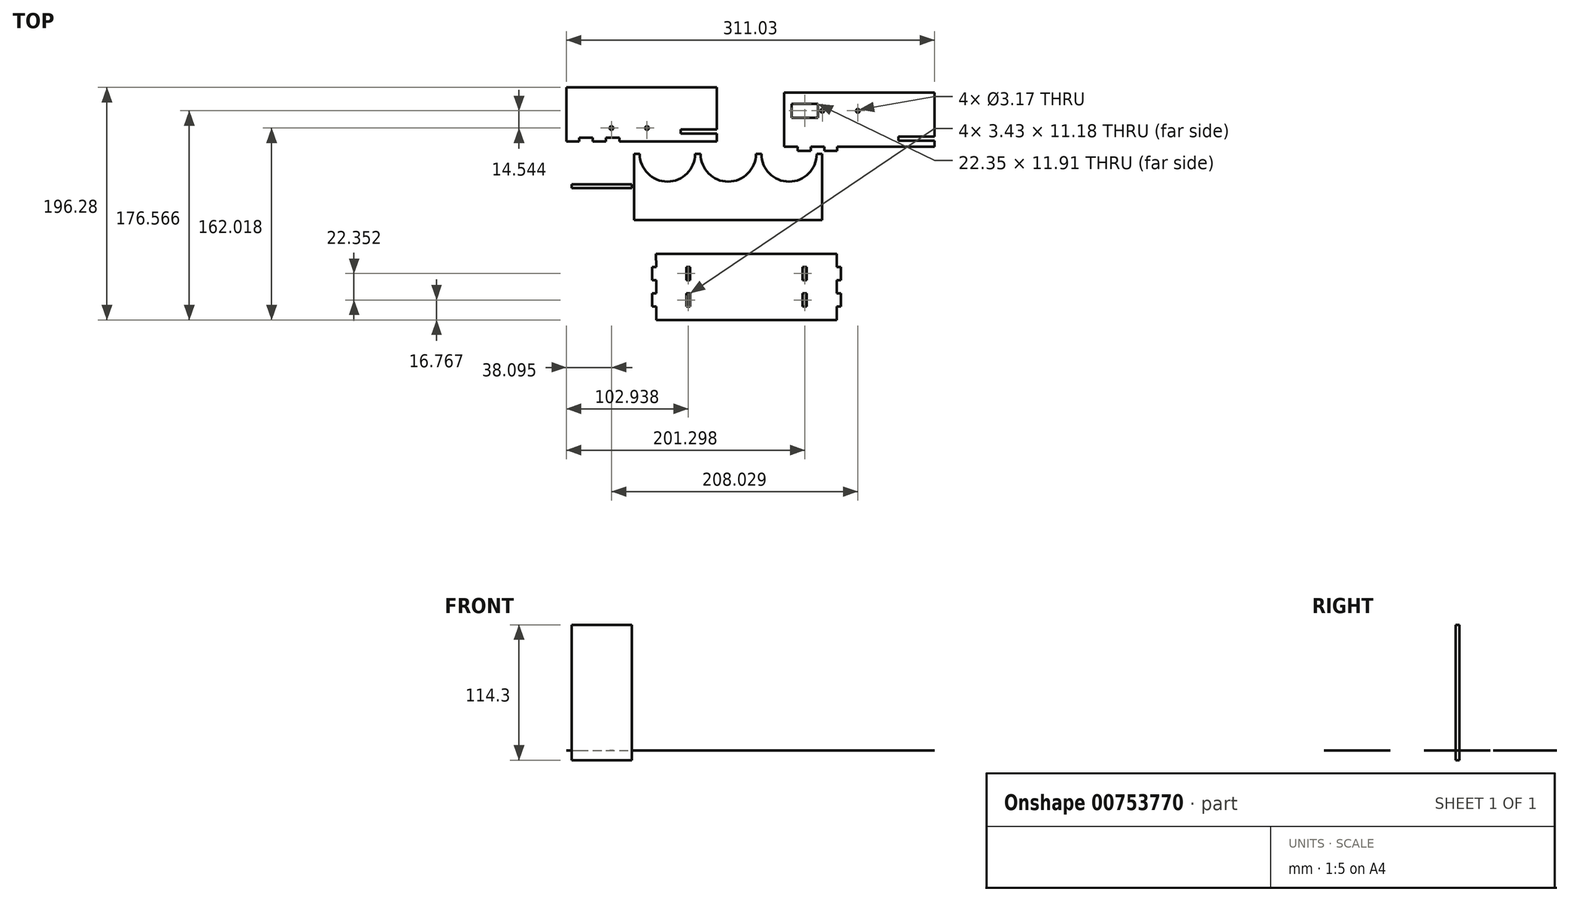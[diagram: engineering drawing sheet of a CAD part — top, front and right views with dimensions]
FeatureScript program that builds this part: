
annotation { "Feature Type Name" : "Feature", "Feature Type Description" : "" }
export const myFeature = defineFeature(function(context is Context, id is Id, definition is map)
    precondition{}
    {
        {
            var Q0;
            Q0=qCreatedBy(makeId("Top.planeOp"),FACE);
            var sketch = newSketch(context, id + "F0", { "sketchPlane" : qUnion([Q0])});
            skLineSegment(sketch, "E0.bottom", {"start": v(-76.72, 25.8) * mm, "end": v(-72.09, 25.8) * mm});
            skLineSegment(sketch, "E0.top", {"start": v(-76.72, -30.08) * mm, "end": v(82.03, -30.08) * mm});
            skLineSegment(sketch, "E0.left", {"start": v(-76.72, 25.8) * mm, "end": v(-76.72, -30.08) * mm});
            skLineSegment(sketch, "E0.right", {"start": v(82.03, 25.8) * mm, "end": v(82.03, -30.08) * mm});
            skArc(sketch, "E1", {"start": v(-20.72, 25.8) * mm, "mid": v(2.65, 2.43) * mm, "end": v(26.02, 25.8) * mm});
            skLineSegment(sketch, "E2.trimOffspring", {"start": v(26.02, 25.8) * mm, "end": v(30.66, 25.8) * mm});
            skArc(sketch, "E3", {"start": v(-72.09, 25.8) * mm, "mid": v(-48.72, 2.43) * mm, "end": v(-25.35, 25.8) * mm});
            skArc(sketch, "E4", {"start": v(30.66, 25.8) * mm, "mid": v(54.02, 2.43) * mm, "end": v(77.4, 25.8) * mm});
            skLineSegment(sketch, "E5.trimOffspring", {"start": v(-25.35, 25.8) * mm, "end": v(-20.72, 25.8) * mm});
            skLineSegment(sketch, "E6.trimOffspring", {"start": v(77.4, 25.8) * mm, "end": v(82.03, 25.8) * mm});
            skSolve(sketch);
        }
        {
            var Q0;
            Q0 = qSketchRegion(id + "F0", true);
            extrude(context, id + "F1", {"entities" : qUnion([Q0]), "depth" : 1 / 203.2 * mm, "offsetDistance" : 25.4 * mm});
        }
        {
            var Q0;
            Q0=qCreatedBy(makeId("Top.planeOp"),FACE);
            var sketch = newSketch(context, id + "F2", { "sketchPlane" : qUnion([Q0])});
            skLineSegment(sketch, "E7.bottom", {"start": v(-134.04, 81.95) * mm, "end": v(-7.04, 81.95) * mm});
            skLineSegment(sketch, "E7.top", {"start": v(-134.04, 36.23) * mm, "end": v(-123.12, 36.23) * mm});
            skLineSegment(sketch, "E7.left", {"start": v(-134.04, 81.95) * mm, "end": v(-134.04, 36.23) * mm});
            skLineSegment(sketch, "E7.right", {"start": v(-7.04, 81.95) * mm, "end": v(-7.04, 46.4) * mm});
            skLineSegment(sketch, "E8.bottom", {"start": v(-7.04, 46.4) * mm, "end": v(-37.52, 46.4) * mm});
            skLineSegment(sketch, "E8.top", {"start": v(-7.04, 42.96) * mm, "end": v(-37.52, 42.96) * mm});
            skLineSegment(sketch, "E8.right", {"start": v(-37.52, 46.4) * mm, "end": v(-37.52, 42.96) * mm});
            skLineSegment(sketch, "E9.trimOffspring", {"start": v(-7.04, 42.96) * mm, "end": v(-7.04, 36.23) * mm});
            skLineSegment(sketch, "E10.top", {"start": v(-123.12, 39.66) * mm, "end": v(-111.7, 39.66) * mm});
            skLineSegment(sketch, "E10.left", {"start": v(-123.12, 36.23) * mm, "end": v(-123.12, 39.66) * mm});
            skLineSegment(sketch, "E10.right", {"start": v(-111.7, 36.23) * mm, "end": v(-111.7, 39.66) * mm});
            skLineSegment(sketch, "E11.top", {"start": v(-100.77, 39.66) * mm, "end": v(-89.34, 39.66) * mm});
            skLineSegment(sketch, "E11.left", {"start": v(-100.77, 36.23) * mm, "end": v(-100.77, 39.66) * mm});
            skLineSegment(sketch, "E11.right", {"start": v(-89.34, 36.23) * mm, "end": v(-89.34, 39.66) * mm});
            skLineSegment(sketch, "E12.trimOffspring", {"start": v(-111.7, 36.23) * mm, "end": v(-100.77, 36.23) * mm});
            skLineSegment(sketch, "E13.trimOffspring", {"start": v(-89.34, 36.23) * mm, "end": v(-78.42, 36.23) * mm});
            skLineSegment(sketch, "E14.trimOffspring", {"start": v(-66.99, 36.23) * mm, "end": v(-7.04, 36.23) * mm});
            skLineSegment(sketch, "E15", {"start": v(-78.42, 36.23) * mm, "end": v(-66.99, 36.23) * mm});
            skCircle(sketch, "E16", {"center": v(-95.94, 47.69) * mm, "radius": 1.59 * mm});
            skCircle(sketch, "E17", {"center": v(-65.94, 47.69) * mm, "radius": 1.59 * mm});
            skSolve(sketch);
        }
        {
            var Q0;
            Q0 = qSketchRegion(id + "F2", true);
            extrude(context, id + "F3", {"entities" : qUnion([Q0]), "depth" : 1 / 203.2 * mm, "offsetDistance" : 25.4 * mm});
        }
        {
            var Q0;
            Q0=qCreatedBy(makeId("Top.planeOp"),FACE);
            var sketch = newSketch(context, id + "F4", { "sketchPlane" : qUnion([Q0])});
            skLineSegment(sketch, "E18.bottom", {"start": v(-58.57, -58.45) * mm, "end": v(94.33, -58.45) * mm});
            skLineSegment(sketch, "E18.top", {"start": v(-58.07, -114.33) * mm, "end": v(94.33, -114.33) * mm});
            skLineSegment(sketch, "E18.left", {"start": v(-61.65, -69.62) * mm, "end": v(-61.65, -80.8) * mm});
            skLineSegment(sketch, "E18.right", {"start": v(97.76, -69.62) * mm, "end": v(97.76, -80.8) * mm});
            skLineSegment(sketch, "E19.top", {"start": v(-61.65, -69.62) * mm, "end": v(-58.22, -69.62) * mm});
            skLineSegment(sketch, "E19.right", {"start": v(-58.57, -58.45) * mm, "end": v(-58.22, -69.62) * mm});
            skLineSegment(sketch, "E20.top", {"start": v(-61.65, -103.15) * mm, "end": v(-58.22, -103.15) * mm});
            skLineSegment(sketch, "E20.right", {"start": v(-58.07, -114.33) * mm, "end": v(-58.22, -103.15) * mm});
            skLineSegment(sketch, "E21.bottom", {"start": v(-61.65, -80.8) * mm, "end": v(-58.22, -80.8) * mm});
            skLineSegment(sketch, "E21.top", {"start": v(-61.65, -91.97) * mm, "end": v(-58.22, -91.97) * mm});
            skLineSegment(sketch, "E21.right", {"start": v(-58.22, -80.8) * mm, "end": v(-58.22, -91.97) * mm});
            skLineSegment(sketch, "E22.trimOffspring", {"start": v(-61.65, -91.97) * mm, "end": v(-61.65, -103.15) * mm});
            skLineSegment(sketch, "E23.top", {"start": v(97.76, -69.62) * mm, "end": v(94.33, -69.62) * mm});
            skLineSegment(sketch, "E23.right", {"start": v(94.33, -58.45) * mm, "end": v(94.33, -69.62) * mm});
            skLineSegment(sketch, "E24.top", {"start": v(97.76, -103.15) * mm, "end": v(94.33, -103.15) * mm});
            skLineSegment(sketch, "E24.right", {"start": v(94.33, -114.33) * mm, "end": v(94.33, -103.15) * mm});
            skLineSegment(sketch, "E25.bottom", {"start": v(97.76, -80.8) * mm, "end": v(94.33, -80.8) * mm});
            skLineSegment(sketch, "E25.top", {"start": v(97.76, -91.97) * mm, "end": v(94.33, -91.97) * mm});
            skLineSegment(sketch, "E25.right", {"start": v(94.33, -80.8) * mm, "end": v(94.33, -91.97) * mm});
            skLineSegment(sketch, "E26.trimOffspring", {"start": v(97.76, -91.97) * mm, "end": v(97.76, -103.15) * mm});
            skLineSegment(sketch, "E27.bottom", {"start": v(-32.82, -69.62) * mm, "end": v(-29.39, -69.62) * mm});
            skLineSegment(sketch, "E27.top", {"start": v(-32.82, -80.8) * mm, "end": v(-29.39, -80.8) * mm});
            skLineSegment(sketch, "E27.left", {"start": v(-32.82, -69.62) * mm, "end": v(-32.82, -80.8) * mm});
            skLineSegment(sketch, "E27.right", {"start": v(-29.39, -69.62) * mm, "end": v(-29.39, -80.8) * mm});
            skLineSegment(sketch, "E28.bottom", {"start": v(-32.82, -91.97) * mm, "end": v(-29.39, -91.97) * mm});
            skLineSegment(sketch, "E28.top", {"start": v(-32.82, -103.15) * mm, "end": v(-29.39, -103.15) * mm});
            skLineSegment(sketch, "E28.left", {"start": v(-32.82, -91.97) * mm, "end": v(-32.82, -103.15) * mm});
            skLineSegment(sketch, "E28.right", {"start": v(-29.39, -91.97) * mm, "end": v(-29.39, -103.15) * mm});
            skLineSegment(sketch, "E29.bottom", {"start": v(68.93, -69.62) * mm, "end": v(65.5, -69.62) * mm});
            skLineSegment(sketch, "E29.top", {"start": v(68.93, -80.8) * mm, "end": v(65.5, -80.8) * mm});
            skLineSegment(sketch, "E29.left", {"start": v(68.93, -69.62) * mm, "end": v(68.93, -80.8) * mm});
            skLineSegment(sketch, "E29.right", {"start": v(65.5, -69.62) * mm, "end": v(65.5, -80.8) * mm});
            skLineSegment(sketch, "E30.bottom", {"start": v(68.93, -91.97) * mm, "end": v(65.5, -91.97) * mm});
            skLineSegment(sketch, "E30.top", {"start": v(68.93, -103.15) * mm, "end": v(65.5, -103.15) * mm});
            skLineSegment(sketch, "E30.left", {"start": v(68.93, -91.97) * mm, "end": v(68.93, -103.15) * mm});
            skLineSegment(sketch, "E30.right", {"start": v(65.5, -91.97) * mm, "end": v(65.5, -103.15) * mm});
            skSolve(sketch);
        }
        {
            var Q0;
            Q0 = qSketchRegion(id + "F4", true);
            extrude(context, id + "F5", {"entities" : qUnion([Q0]), "depth" : 1 / 203.2 * mm, "offsetDistance" : 25.4 * mm});
        }
        {
            var Q0;
            Q0=qCreatedBy(makeId("Top.planeOp"),FACE);
            var sketch = newSketch(context, id + "F6", { "sketchPlane" : qUnion([Q0])});
            skLineSegment(sketch, "E31.bottom", {"start": v(49.99, 77.71) * mm, "end": v(176.99, 77.71) * mm});
            skLineSegment(sketch, "E31.top", {"start": v(49.99, 32) * mm, "end": v(61.42, 32) * mm});
            skLineSegment(sketch, "E31.left", {"start": v(49.99, 77.71) * mm, "end": v(49.99, 32) * mm});
            skLineSegment(sketch, "E31.right", {"start": v(176.99, 77.71) * mm, "end": v(176.99, 40.57) * mm});
            skLineSegment(sketch, "E32.bottom", {"start": v(176.99, 40.57) * mm, "end": v(146.5, 40.57) * mm});
            skLineSegment(sketch, "E32.top", {"start": v(176.99, 37.14) * mm, "end": v(146.5, 37.14) * mm});
            skLineSegment(sketch, "E32.right", {"start": v(146.5, 40.57) * mm, "end": v(146.5, 37.14) * mm});
            skLineSegment(sketch, "E33.trimOffspring", {"start": v(176.99, 37.14) * mm, "end": v(176.99, 32) * mm});
            skLineSegment(sketch, "E34.top", {"start": v(61.42, 28.56) * mm, "end": v(72.34, 28.56) * mm});
            skLineSegment(sketch, "E34.left", {"start": v(61.42, 32) * mm, "end": v(61.42, 28.56) * mm});
            skLineSegment(sketch, "E34.right", {"start": v(72.34, 32) * mm, "end": v(72.34, 28.56) * mm});
            skLineSegment(sketch, "E35.top", {"start": v(83.77, 28.56) * mm, "end": v(94.7, 28.56) * mm});
            skLineSegment(sketch, "E35.left", {"start": v(83.77, 32) * mm, "end": v(83.77, 28.56) * mm});
            skLineSegment(sketch, "E35.right", {"start": v(94.7, 32) * mm, "end": v(94.7, 28.56) * mm});
            skLineSegment(sketch, "E36.trimOffspring", {"start": v(94.7, 32) * mm, "end": v(176.99, 32) * mm});
            skLineSegment(sketch, "E37.trimOffspring", {"start": v(72.34, 32) * mm, "end": v(83.77, 32) * mm});
            skCircle(sketch, "E38", {"center": v(82.08, 62.23) * mm, "radius": 1.59 * mm});
            skCircle(sketch, "E39", {"center": v(112.08, 62.23) * mm, "radius": 1.59 * mm});
            skLineSegment(sketch, "E40.bottom", {"start": v(56.08, 68.19) * mm, "end": v(78.43, 68.19) * mm});
            skLineSegment(sketch, "E40.top", {"start": v(56.08, 56.28) * mm, "end": v(78.43, 56.28) * mm});
            skLineSegment(sketch, "E40.left", {"start": v(56.08, 68.19) * mm, "end": v(56.08, 56.28) * mm});
            skLineSegment(sketch, "E40.right", {"start": v(78.43, 68.19) * mm, "end": v(78.43, 56.28) * mm});
            skSolve(sketch);
        }
        {
            var Q0;
            Q0 = qSketchRegion(id + "F6", true);
            extrude(context, id + "F7", {"entities" : qUnion([Q0]), "depth" : 1 / 203.2 * mm, "offsetDistance" : 25.4 * mm});
        }
        {
            var Q0;
            Q0=qCreatedBy(makeId("Front.planeOp"),FACE);
            var sketch = newSketch(context, id + "F8", { "sketchPlane" : qUnion([Q0])});
            skLineSegment(sketch, "E41.bottom", {"start": v(-129.48, 106.18) * mm, "end": v(-78.68, 106.18) * mm});
            skLineSegment(sketch, "E41.top", {"start": v(-129.48, -8.12) * mm, "end": v(-78.68, -8.12) * mm});
            skLineSegment(sketch, "E41.left", {"start": v(-129.48, 106.18) * mm, "end": v(-129.48, -8.12) * mm});
            skLineSegment(sketch, "E41.right", {"start": v(-78.68, 106.18) * mm, "end": v(-78.68, -8.12) * mm});
            skSolve(sketch);
        }
        {
            var Q0;
            Q0 = qSketchRegion(id + "F8", true);
            extrude(context, id + "F9", {"entities" : qUnion([Q0]), "depth" : 3.17 * mm, "offsetDistance" : 25.4 * mm});
        }
    });
